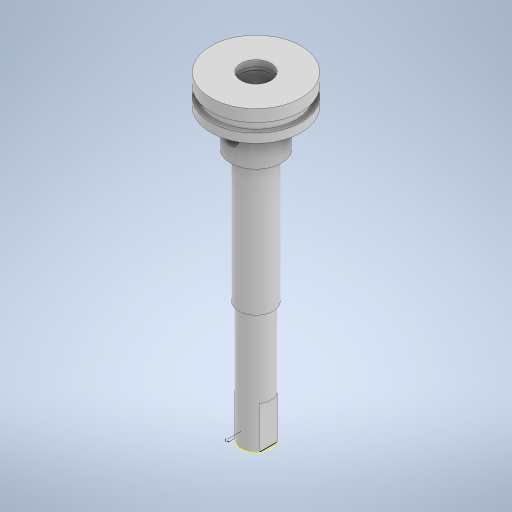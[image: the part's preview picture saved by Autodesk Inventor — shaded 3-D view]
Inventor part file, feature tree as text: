
AUTODESK INVENTOR PART (.ipt)
format: ipt  version: 2023 (Build 270158000, 158)  size: 317,440 bytes
history: native  units: mm
features: sketch x3, extrude x2, revolve x1
ambient origin geometry x8: Origin, YZ Plane, XZ Plane, XY Plane, X Axis, Y Axis, Z Axis, Center Point
bodies: Solido1 (feature_tree)
feature tree (6):
  revolve  "Rivoluzione1"
  extrude  "Estrusione1"  Depth=10.0mm
  sketch  "Schizzo3"
  extrude  "Estrusione2"  Depth=11.5mm
  sketch  "Schizzo1"
  sketch  "Schizzo2"
